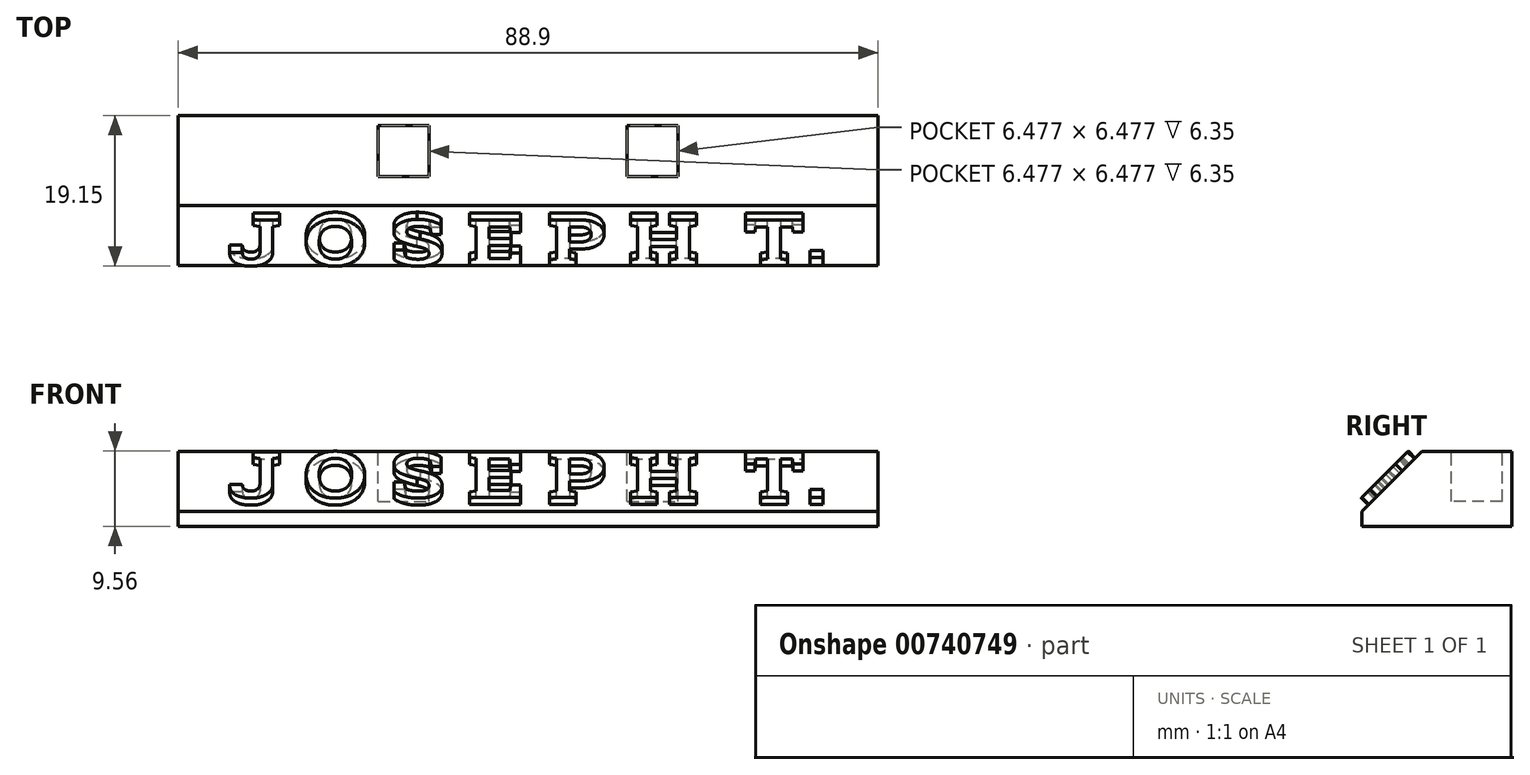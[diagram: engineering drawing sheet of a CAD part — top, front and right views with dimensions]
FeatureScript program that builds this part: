
annotation { "Feature Type Name" : "Feature", "Feature Type Description" : "" }
export const myFeature = defineFeature(function(context is Context, id is Id, definition is map)
    precondition{}
    {
        {
            var Q0;
            Q0=qCreatedBy(makeId("Front.planeOp"),FACE);
            var sketch = newSketch(context, id + "F0", { "sketchPlane" : qUnion([Q0])});
            skLineSegment(sketch, "E0.bottom", {"start": v(0, 0) * mm, "end": v(88.9, 0) * mm});
            skLineSegment(sketch, "E0.top", {"start": v(0, 9.53) * mm, "end": v(88.9, 9.53) * mm});
            skLineSegment(sketch, "E0.left", {"start": v(0, 0) * mm, "end": v(0, 9.53) * mm});
            skLineSegment(sketch, "E0.right", {"start": v(88.9, 0) * mm, "end": v(88.9, 9.53) * mm});
            skSolve(sketch);
        }
        {
            var Q0;
            Q0=makeQuery(id+"F0.imprint","IMPRINT",FACE,{"disambiguationData":[TD([[makeQuery(id+"F0.imprint","IMPRINT",EDGE,{"derivedFrom":sQuery(id+"F0.wireOp",EDGE,"E0.bottom")}),1.0]])]});
            extrude(context, id + "F1", {"entities" : qUnion([Q0]), "depth" : 19.05 * mm, "offsetDistance" : 25.4 * mm});
        }
        {
            var Q0;
            Q0=makeQuery(id+"F1.opExtrude","CAP_EDGE",EDGE,{"disambiguationData":[OSD([sQuery(id+"F0.wireOp",EDGE,"E0.top")])],"isStart":false});
            chamfer(context, id + "F2", {"entities" : qUnion([Q0]), "width" : 7.62 * mm, "tangentPropagation" : true});
        }
        {
            var Q0;
            Q0=makeQuery(id+"F2.opChamfer","BLEND_FACE",FACE,{"disambiguationData":[OSD([sQuery(id+"F0.wireOp",EDGE,"E0.top")])]});
            var sketch = newSketch(context, id + "F3", { "sketchPlane" : qUnion([Q0])});
            skText(sketch, "E1", { "text": "J O S E P H  T.", "fontName": "RobotoSlab-Bold.ttf"});
            skLineSegment(sketch, "E2", {"start": v(44.45, -1.35) * mm, "end": v(44.45, -12.12) * mm});
            const initialGuessF3  = {"E1": [0.00635, -0.01088, 1, 0, 0.0083]};
            skSetInitialGuess(sketch, initialGuessF3);
            skSolve(sketch);
        }
        {
            var Q0;
            Q0 = qSketchRegion(id + "F3", true);
            extrude(context, id + "F4", {"entities" : qUnion([Q0]), "operationType" : NewBodyOperationType.ADD, "depth" : 1.27 * mm, "offsetDistance" : 25.4 * mm});
        }
        {
            var Q0;
            Q0=makeQuery(id+"F1.opExtrude","SWEPT_FACE",FACE,{"disambiguationData":[OSD([sQuery(id+"F0.wireOp",EDGE,"E0.top")])]});
            var sketch = newSketch(context, id + "F5", { "sketchPlane" : qUnion([Q0])});
            skLineSegment(sketch, "E3.bottom", {"start": v(25.4, -1.27) * mm, "end": v(31.88, -1.27) * mm});
            skLineSegment(sketch, "E3.top", {"start": v(25.4, -7.75) * mm, "end": v(31.88, -7.75) * mm});
            skLineSegment(sketch, "E3.left", {"start": v(25.4, -1.27) * mm, "end": v(25.4, -7.75) * mm});
            skLineSegment(sketch, "E3.right", {"start": v(31.88, -1.27) * mm, "end": v(31.88, -7.75) * mm});
            skLineSegment(sketch, "E4.bottom", {"start": v(57.02, -1.27) * mm, "end": v(63.5, -1.27) * mm});
            skLineSegment(sketch, "E4.top", {"start": v(57.02, -7.75) * mm, "end": v(63.5, -7.75) * mm});
            skLineSegment(sketch, "E4.left", {"start": v(57.02, -1.27) * mm, "end": v(57.02, -7.75) * mm});
            skLineSegment(sketch, "E4.right", {"start": v(63.5, -1.27) * mm, "end": v(63.5, -7.75) * mm});
            skLineSegment(sketch, "E5", {"start": v(25.4, -4.5) * mm, "end": v(31.88, -4.5) * mm});
            skLineSegment(sketch, "E6", {"start": v(57.02, -4.5) * mm, "end": v(63.5, -4.5) * mm});
            skPoint(sketch, "E7.orphan", {"position": v(0, -5.72) * mm});
            skPoint(sketch, "E8.orphan", {"position": v(88.9, -5.72) * mm});
            skSolve(sketch);
        }
        {
            var Q0;
            {var subQ0=sQuery(id+"F5.wireOp",EDGE,"E3.bottom");Q0=makeQuery(id+"F5.imprint","IMPRINT",FACE,{"disambiguationData":[TD([[makeQuery(id+"F5.imprint","IMPRINT",EDGE,{"derivedFrom":subQ0}),-1.0]])]});}
            var Q1;
            {var subQ0=sQuery(id+"F5.wireOp",EDGE,"E3.top");Q1=makeQuery(id+"F5.imprint","IMPRINT",FACE,{"disambiguationData":[TD([[makeQuery(id+"F5.imprint","IMPRINT",EDGE,{"derivedFrom":subQ0}),1.0]])]});}
            var Q2;
            {var subQ0=sQuery(id+"F5.wireOp",EDGE,"E4.bottom");Q2=makeQuery(id+"F5.imprint","IMPRINT",FACE,{"disambiguationData":[TD([[makeQuery(id+"F5.imprint","IMPRINT",EDGE,{"derivedFrom":subQ0}),-1.0]])]});}
            var Q3;
            {var subQ0=sQuery(id+"F5.wireOp",EDGE,"E4.top");Q3=makeQuery(id+"F5.imprint","IMPRINT",FACE,{"disambiguationData":[TD([[makeQuery(id+"F5.imprint","IMPRINT",EDGE,{"derivedFrom":subQ0}),1.0]])]});}
            extrude(context, id + "F6", {"entities" : qUnion([Q0, Q1, Q2, Q3]), "operationType" : NewBodyOperationType.REMOVE, "oppositeDirection" : true, "depth" : 6.35 * mm, "offsetDistance" : 25.4 * mm});
        }
    });
